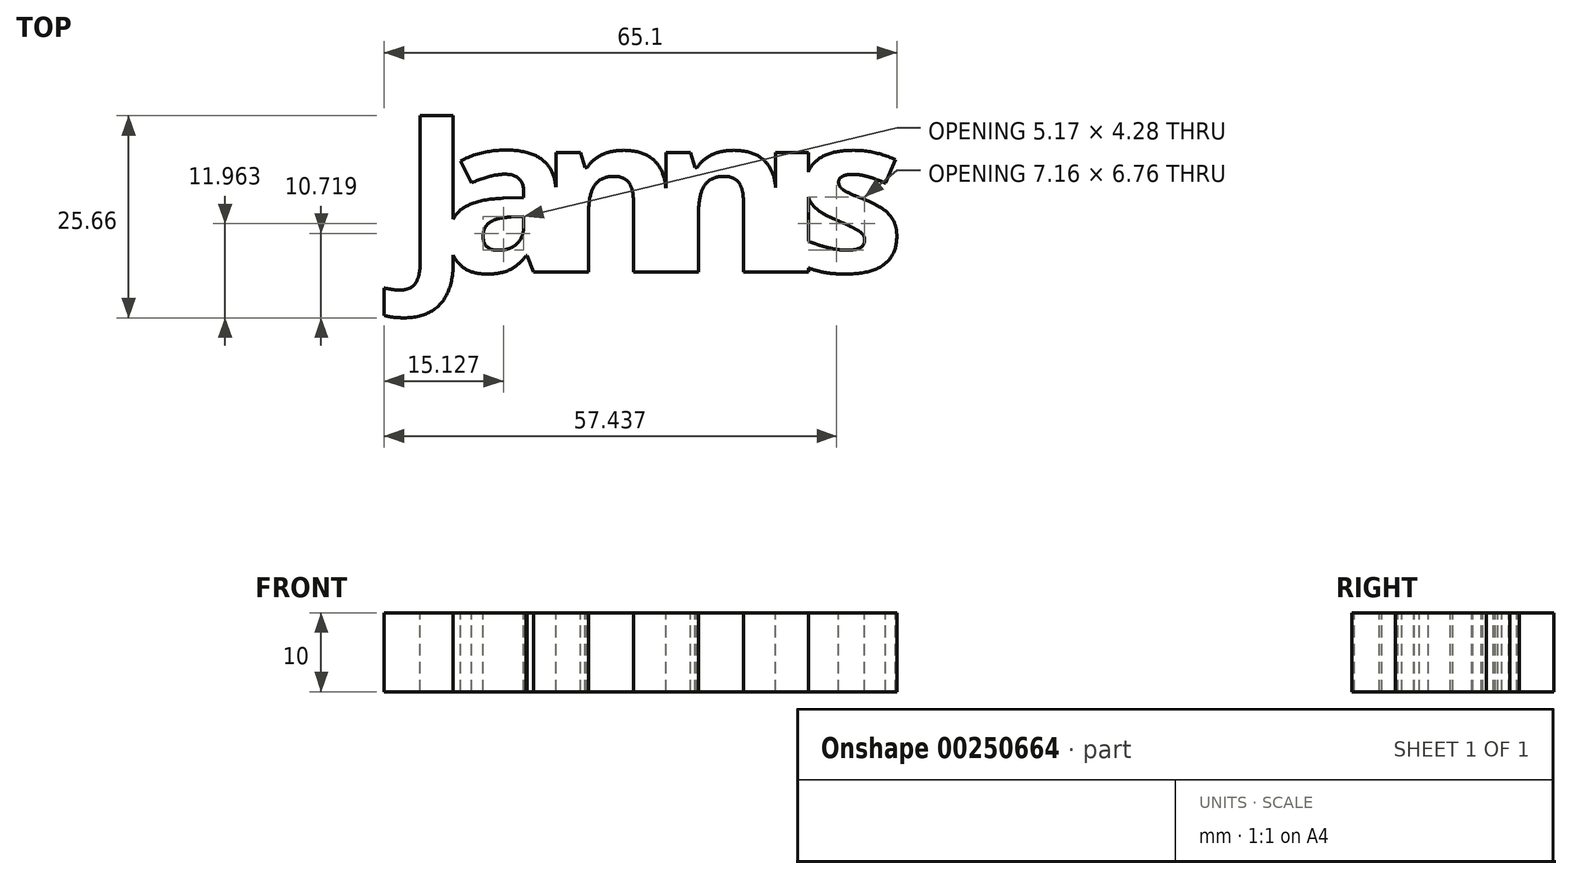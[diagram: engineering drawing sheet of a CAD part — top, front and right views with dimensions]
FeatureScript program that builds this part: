
annotation { "Feature Type Name" : "Feature", "Feature Type Description" : "" }
export const myFeature = defineFeature(function(context is Context, id is Id, definition is map)
    precondition{}
    {
        {
            var Q0;
            Q0=qCreatedBy(makeId("Top.planeOp"),FACE);
            var sketch = newSketch(context, id + "F0", { "sketchPlane" : qUnion([Q0])});
            skText(sketch, "E0", { "text": "J", "fontName": "OpenSans-Bold.ttf"});
            skText(sketch, "E1", { "text": "a", "fontName": "OpenSans-Bold.ttf"});
            skText(sketch, "E2", { "text": "n", "fontName": "OpenSans-Bold.ttf"});
            skText(sketch, "E3", { "text": "n", "fontName": "OpenSans-Bold.ttf"});
            skText(sketch, "E4", { "text": "i", "fontName": "OpenSans-Bold.ttf"});
            skText(sketch, "E5", { "text": "s", "fontName": "OpenSans-Bold.ttf"});
            const initialGuessF0  = {"E0": [-0.11764, 0.02526, 1, 0, 0.02], "E1": [-0.11257, 0.02526, 1, 0, 0.02], "E2": [-0.10008, 0.02526, 1, 0, 0.02], "E3": [-0.08611, 0.02526, 1, 0, 0.02], "E4": [-0.07215, 0.02526, 1, 0, 0.02], "E5": [-0.06735, 0.02526, 1, 0, 0.02]};
            skSetInitialGuess(sketch, initialGuessF0);
            skSolve(sketch);
        }
        {
            var Q0;
            Q0 = qSketchRegion(id + "F0", true);
            extrude(context, id + "F1", {"entities" : qUnion([Q0]), "oppositeDirection" : true, "depth" : 10 * mm});
        }
        {
            var Q0;
            Q0=makeQuery(id+"F1.opExtrude","CAP_FACE",FACE,{"disambiguationData":[OSD([sQuery(id+"F0.wireOp",EDGE,"E4.sketch_text.stroke-0"),sQuery(id+"F0.wireOp",EDGE,"E4.sketch_text.stroke-1"),sQuery(id+"F0.wireOp",EDGE,"E4.sketch_text.stroke-2"),sQuery(id+"F0.wireOp",EDGE,"E4.sketch_text.stroke-3"),sQuery(id+"F0.wireOp",EDGE,"E4.sketch_text.stroke-4")])],"isStart":true});
            extrude(context, id + "F2", {"entities" : qUnion([Q0]), "operationType" : NewBodyOperationType.REMOVE, "oppositeDirection" : true, "depth" : 25 * mm});
        }
    });
